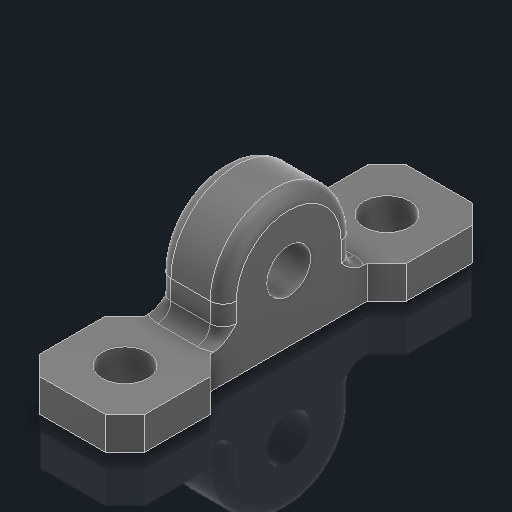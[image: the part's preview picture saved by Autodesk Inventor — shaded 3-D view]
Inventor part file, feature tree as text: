
AUTODESK INVENTOR PART (.ipt)
format: ipt  version: 2023.2 (Build 272271030, 271C)  size: 225,792 bytes
history: native  units: in
note: dims shown in document units (in); Inventor stores cm internally (conversion verified against a paired STEP export)
features: other x3, sketch x3
ambient origin geometry x8: Origin, YZ Plane, XZ Plane, XY Plane, X Axis, Y Axis, Z Axis, Center Point
bodies: Solid1 (feature_tree)
feature tree (6):
  other  "LS Pillow Bearing Block.ipt"
  other  "Solid1::LS Pillow Bearing Block.ipt"
  other  "TaggingFeature1"
  sketch  "Sketch1"  dims[d0=0.3937in]
  sketch  "Sketch2"
  sketch  "Sketch3"
